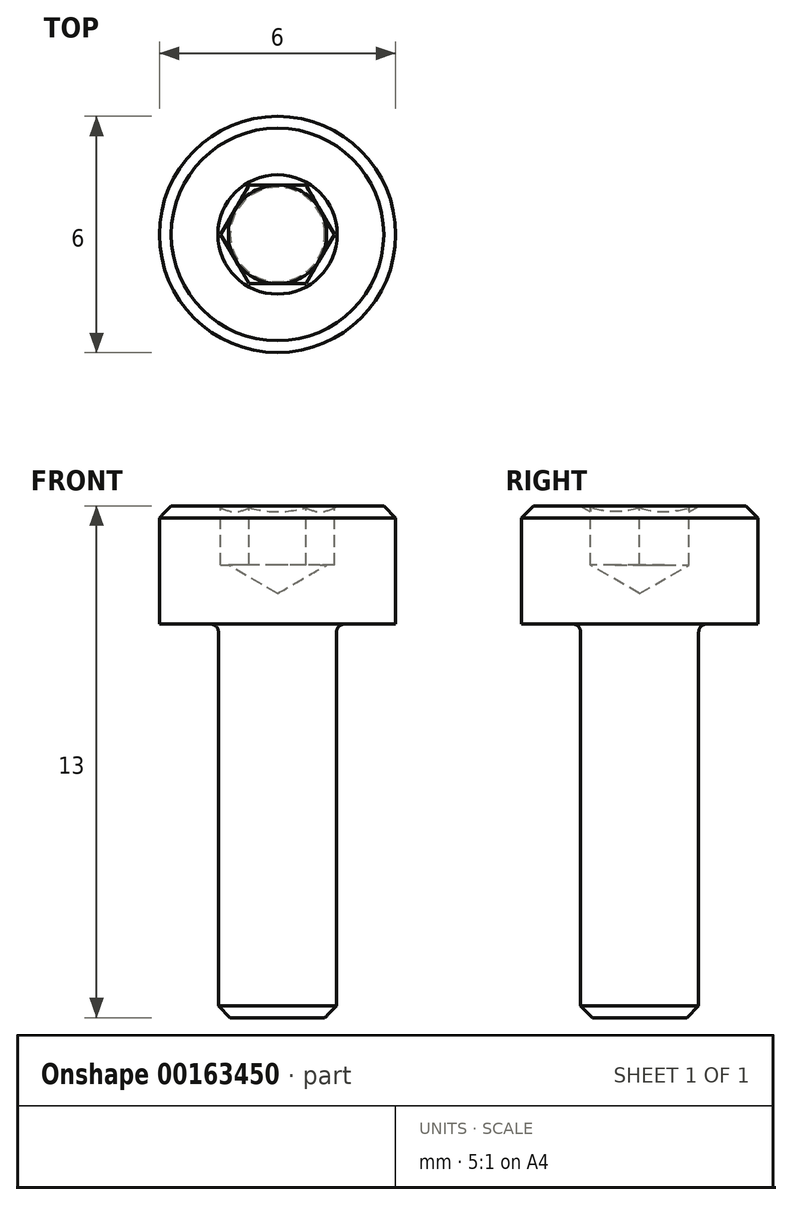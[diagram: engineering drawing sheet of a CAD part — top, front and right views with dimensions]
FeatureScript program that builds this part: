
annotation { "Feature Type Name" : "Feature", "Feature Type Description" : "" }
export const myFeature = defineFeature(function(context is Context, id is Id, definition is map)
    precondition{}
    {
        {
            var Q0;
            Q0=qCreatedBy(makeId("Front.planeOp"),FACE);
            var sketch = newSketch(context, id + "F0", { "sketchPlane" : qUnion([Q0])});
            skLineSegment(sketch, "E0", {"start": v(0, 3) * mm, "end": v(3, 3) * mm});
            skLineSegment(sketch, "E1", {"start": v(3, 3) * mm, "end": v(3, 0) * mm});
            skLineSegment(sketch, "E2", {"start": v(3, 0) * mm, "end": v(1.5, 0) * mm});
            skLineSegment(sketch, "E3", {"start": v(1.5, 0) * mm, "end": v(1.5, -10) * mm});
            skLineSegment(sketch, "E4", {"start": v(1.5, -10) * mm, "end": v(0, -10) * mm});
            skLineSegment(sketch, "E5", {"start": v(0, -10) * mm, "end": v(0, 3) * mm});
            skLineSegment(sketch, "E6.MirrorCS", {"start": v(0, 3) * mm, "end": v(-3, 3) * mm, "construction": true});
            skLineSegment(sketch, "E7.MirrorCS", {"start": v(-3, 3) * mm, "end": v(-3, 0) * mm, "construction": true});
            skLineSegment(sketch, "E8.MirrorCS", {"start": v(-3, 0) * mm, "end": v(-1.5, 0) * mm, "construction": true});
            skLineSegment(sketch, "E9.MirrorCS", {"start": v(-1.5, 0) * mm, "end": v(-1.5, -10) * mm, "construction": true});
            skLineSegment(sketch, "E10.MirrorCS", {"start": v(-1.5, -10) * mm, "end": v(0, -10) * mm, "construction": true});
            skSolve(sketch);
        }
        {
            var Q0;
            Q0 = qSketchRegion(id + "F0", true);
            var Q1;
            Q1=sQuery(id+"F0.wireOp",EDGE,"E5");
            revolve(context, id + "F1", {"entities" : qUnion([Q0]), "axis" : qUnion([Q1]), "revolveType" : RevolveType.FULL});
        }
        {
            var Q0;
            Q0=qCreatedBy(makeId("Front.planeOp"),FACE);
            var sketch = newSketch(context, id + "F2", { "sketchPlane" : qUnion([Q0])});
            skLineSegment(sketch, "E11", {"start": v(0, 3) * mm, "end": v(0, 0.78) * mm});
            skLineSegment(sketch, "E12", {"start": v(0, 0.78) * mm, "end": v(1.25, 1.5) * mm});
            skLineSegment(sketch, "E13", {"start": v(1.25, 1.5) * mm, "end": v(1.25, 2.85) * mm});
            skLineSegment(sketch, "E14", {"start": v(1.25, 2.85) * mm, "end": v(1.52, 3) * mm});
            skLineSegment(sketch, "E15", {"start": v(1.52, 3) * mm, "end": v(0, 3) * mm});
            skLineSegment(sketch, "E16.MirrorCS", {"start": v(0, 0.78) * mm, "end": v(-1.25, 1.5) * mm, "construction": true});
            skLineSegment(sketch, "E17.MirrorCS", {"start": v(-1.25, 1.5) * mm, "end": v(-1.25, 2.85) * mm, "construction": true});
            skLineSegment(sketch, "E18.MirrorCS", {"start": v(-1.25, 2.85) * mm, "end": v(-1.52, 3) * mm, "construction": true});
            skLineSegment(sketch, "E19.MirrorCS", {"start": v(-1.52, 3) * mm, "end": v(0, 3) * mm, "construction": true});
            skSolve(sketch);
        }
        {
            var Q0;
            Q0 = qSketchRegion(id + "F2", true);
            var Q1;
            Q1=sQuery(id+"F2.wireOp",EDGE,"E11");
            revolve(context, id + "F3", {"operationType" : NewBodyOperationType.REMOVE, "entities" : qUnion([Q0]), "axis" : qUnion([Q1]), "revolveType" : RevolveType.FULL, "oppositeDirection" : true});
        }
        {
            var Q0;
            Q0=makeQuery(id+"F1.opRevolve","SWEPT_FACE",FACE,{"disambiguationData":[OSD([sQuery(id+"F0.wireOp",EDGE,"E0")])]});
            var sketch = newSketch(context, id + "F4", { "sketchPlane" : qUnion([Q0])});
            skCircle(sketch, "E20.cCircle", {"center": v(0, 0) * mm, "radius": 1.44 * mm, "construction": true});
            skLineSegment(sketch, "E20.0", {"start": v(0.72, 1.25) * mm, "end": v(1.44, 0) * mm});
            skLineSegment(sketch, "E20.1", {"start": v(1.44, 0) * mm, "end": v(0.72, -1.25) * mm});
            skLineSegment(sketch, "E20.2", {"start": v(0.72, -1.25) * mm, "end": v(-0.72, -1.25) * mm});
            skLineSegment(sketch, "E20.3", {"start": v(-0.72, -1.25) * mm, "end": v(-1.44, 0) * mm});
            skLineSegment(sketch, "E20.4", {"start": v(-1.44, 0) * mm, "end": v(-0.72, 1.25) * mm});
            skLineSegment(sketch, "E20.5", {"start": v(-0.72, 1.25) * mm, "end": v(0.72, 1.25) * mm});
            skSolve(sketch);
        }
        {
            var Q0;
            Q0 = qSketchRegion(id + "F4", true);
            extrude(context, id + "F5", {"entities" : qUnion([Q0]), "operationType" : NewBodyOperationType.REMOVE, "oppositeDirection" : true, "depth" : 1.5 * mm});
        }
        {
            var Q0;
            Q0=makeQuery(id+"F1.opRevolve","SWEPT_EDGE",EDGE,{"disambiguationData":[OSD([sQuery(id+"F0.wireOp",EDGE,"E0"),sQuery(id+"F0.wireOp",EDGE,"E1")])]});
            var Q1;
            Q1=makeQuery(id+"F1.opRevolve","SWEPT_EDGE",EDGE,{"disambiguationData":[OSD([sQuery(id+"F0.wireOp",EDGE,"E3"),sQuery(id+"F0.wireOp",EDGE,"E4")])]});
            chamfer(context, id + "F6", {"entities" : qUnion([Q0, Q1]), "width" : 0.3 * mm, "tangentPropagation" : true});
        }
        {
            var Q0;
            Q0=makeQuery(id+"F1.opRevolve","SWEPT_EDGE",EDGE,{"disambiguationData":[OSD([sQuery(id+"F0.wireOp",EDGE,"E2"),sQuery(id+"F0.wireOp",EDGE,"E3")])]});
            fillet(context, id + "F7", {"entities" : qUnion([Q0]), "radius" : 0.2 * mm, "tangentPropagation" : true, "allowEdgeOverflow" : false});
        }
    });
